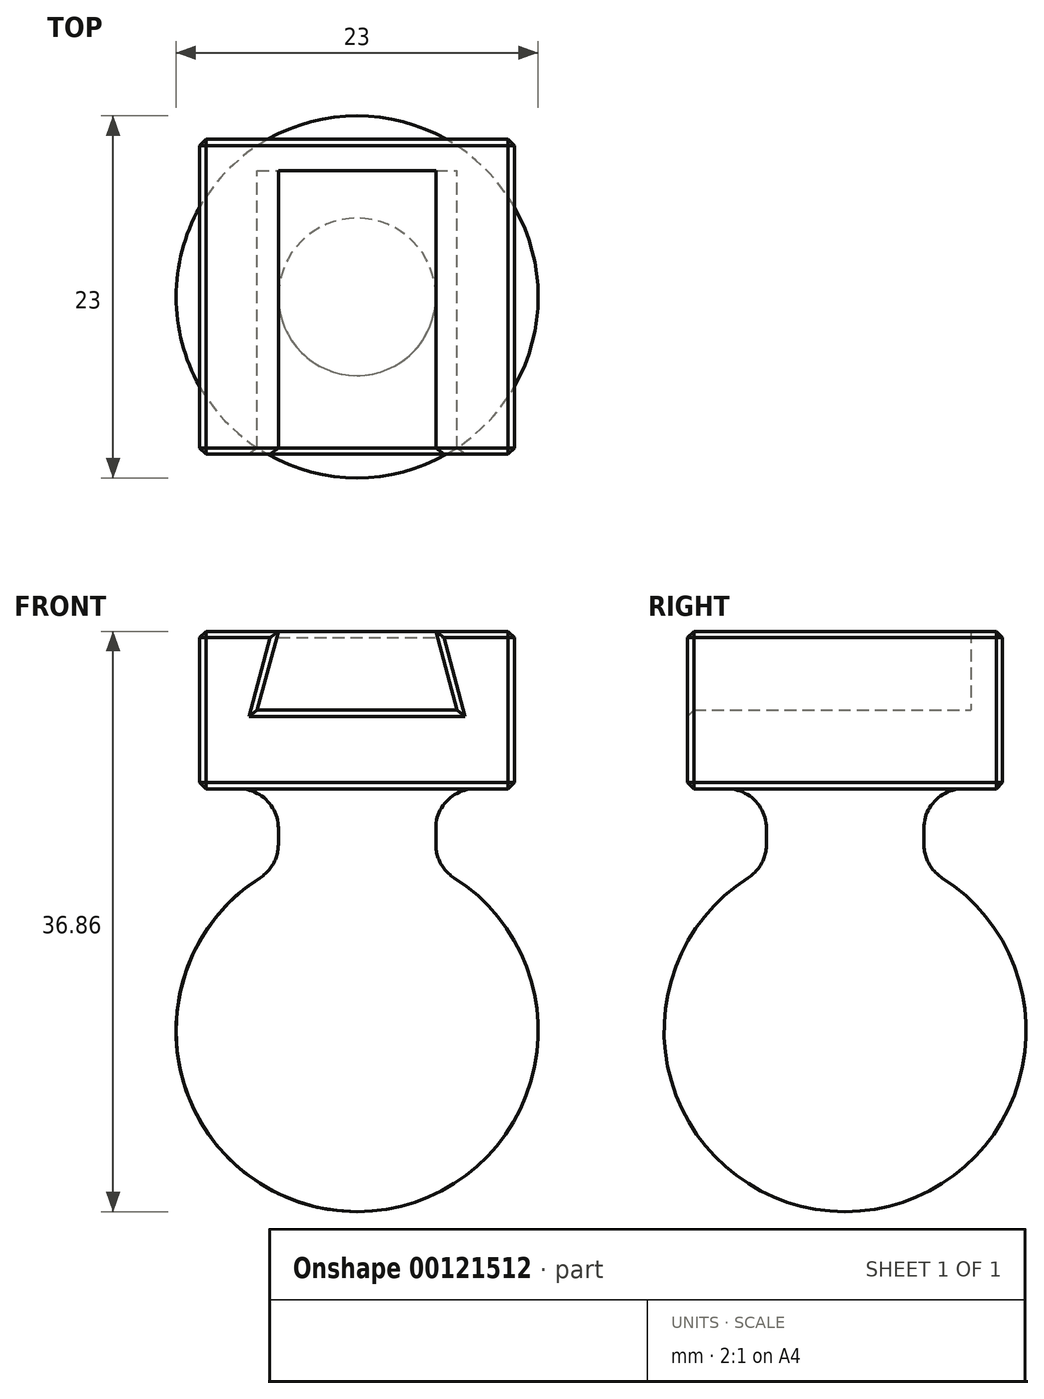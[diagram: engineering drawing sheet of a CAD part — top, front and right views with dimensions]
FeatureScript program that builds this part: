
annotation { "Feature Type Name" : "Feature", "Feature Type Description" : "" }
export const myFeature = defineFeature(function(context is Context, id is Id, definition is map)
    precondition{}
    {
        {
            assignVariable(context, id + "F0", {"name" : "PrintOffset", "anyValue" : 0.4});
        }
        {
            assignVariable(context, id + "F1", {"name" : "DovetailBackstopDepth", "anyValue" : 2});
        }
        {
            assignVariable(context, id + "F2", {"name" : "DovetailDepth", "anyValue" : 20});
        }
        {
            var Q0;
            Q0=qCreatedBy(makeId("Front.planeOp"),FACE);
            var sketch = newSketch(context, id + "F3", { "sketchPlane" : qUnion([Q0])});
            skCircle(sketch, "E0", {"center": v(0, 11.5) * mm, "radius": 11.5 * mm});
            skLineSegment(sketch, "E1", {"start": v(5, 21.86) * mm, "end": v(5, 26.86) * mm});
            skLineSegment(sketch, "E2", {"start": v(0, 26.86) * mm, "end": v(0, 62.06) * mm, "construction": true});
            skLineSegment(sketch, "E3.MirrorCS", {"start": v(-5, 21.86) * mm, "end": v(-5, 26.86) * mm});
            skLineSegment(sketch, "E4", {"start": v(-10, 26.86) * mm, "end": v(10, 26.86) * mm});
            skPoint(sketch, "E5", {"position": v(0, 26.86) * mm});
            skLineSegment(sketch, "E6", {"start": v(0, 26.86) * mm, "end": v(0, 0) * mm});
            skLineSegment(sketch, "E7", {"start": v(-6.34, 31.86) * mm, "end": v(6.34, 31.86) * mm});
            skLineSegment(sketch, "E8", {"start": v(-10, 26.86) * mm, "end": v(-10, 36.86) * mm});
            skLineSegment(sketch, "E9", {"start": v(-10, 36.86) * mm, "end": v(-5, 36.86) * mm});
            skLineSegment(sketch, "E10", {"start": v(-5, 36.86) * mm, "end": v(-6.34, 31.86) * mm});
            skLineSegment(sketch, "E11.MirrorCS", {"start": v(5, 36.86) * mm, "end": v(6.34, 31.86) * mm});
            skLineSegment(sketch, "E12.MirrorCS", {"start": v(10, 26.86) * mm, "end": v(10, 36.86) * mm});
            skLineSegment(sketch, "E13.MirrorCS", {"start": v(10, 36.86) * mm, "end": v(5, 36.86) * mm});
            skLineSegment(sketch, "E14", {"start": v(-5, 36.86) * mm, "end": v(5, 36.86) * mm});
            skSolve(sketch);
        }
        {
            var Q0;
            {var subQ2=sQuery(id+"F3.wireOp",EDGE,"E6");Q0=makeQuery(id+"F3.imprint","IMPRINT",FACE,{"disambiguationData":[TD([[makeQuery(id+"F3.imprint","IMPRINT",EDGE,{"derivedFrom":subQ2}),-1.0]])]});}
            var Q1;
            Q1=sQuery(id+"F3.wireOp",EDGE,"E6");
            revolve(context, id + "F4", {"entities" : qUnion([Q0]), "axis" : qUnion([Q1]), "revolveType" : RevolveType.FULL});
        }
        {
            var Q0;
            {var subQ0=sQuery(id+"F3.wireOp",EDGE,"E3.MirrorCS");Q0=makeQuery(id+"F3.imprint","IMPRINT",FACE,{"disambiguationData":[TD([[makeQuery(id+"F3.imprint","IMPRINT",EDGE,{"derivedFrom":subQ0}),-1.0]])]});}
            var Q1;
            Q1=sQuery(id+"F3.wireOp",EDGE,"E6");
            revolve(context, id + "F5", {"operationType" : NewBodyOperationType.ADD, "entities" : qUnion([Q0]), "axis" : qUnion([Q1]), "revolveType" : RevolveType.FULL});
        }
        {
            var Q0;
            Q0=makeQuery(id+"F3.imprint","IMPRINT",FACE,{"disambiguationData":[TD([[makeQuery(id+"F3.imprint","IMPRINT",EDGE,{"derivedFrom":sQuery(id+"F3.wireOp",EDGE,"E7")}),-1.0]])]});
            extrude(context, id + "F6", {"entities" : qUnion([Q0]), "operationType" : NewBodyOperationType.ADD, "endBound" : BoundingType.SYMMETRIC, "depth" : (getVariable(context, 'DovetailDepth')) * mm});
        }
        {
            var Q0;
            Q0=makeQuery(id+"F3.imprint","IMPRINT",FACE,{"disambiguationData":[TD([[makeQuery(id+"F3.imprint","IMPRINT",EDGE,{"derivedFrom":sQuery(id+"F3.wireOp",EDGE,"E7")}),1.0]])]});
            extrude(context, id + "F7", {"entities" : qUnion([Q0]), "operationType" : NewBodyOperationType.ADD, "oppositeDirection" : true, "depth" : (getVariable(context, 'DovetailDepth') / 2) * mm, "hasSecondDirection" : true, "secondDirectionOppositeDirection" : true, "secondDirectionDepth" : (getVariable(context, 'DovetailDepth') / 2 - getVariable(context, 'DovetailBackstopDepth')) * mm});
        }
        {
            var Q0;
            Q0=makeQuery(id+"F5.opRevolve","SWEPT_FACE",FACE,{"disambiguationData":[OSD([sQuery(id+"F3.wireOp",EDGE,"E3.MirrorCS")])]});
            fillet(context, id + "F9", {"entities" : qUnion([Q0]), "radius" : 2.5 * mm, "tangentPropagation" : true, "allowEdgeOverflow" : false});
        }
        {
            var Q0;
            Q0=makeQuery(id+"F6.opExtrude","CAP_FACE",FACE,{"disambiguationData":[OSD([sQuery(id+"F3.wireOp",EDGE,"E4"),sQuery(id+"F3.wireOp",EDGE,"E7"),sQuery(id+"F3.wireOp",EDGE,"E8"),sQuery(id+"F3.wireOp",EDGE,"E9"),sQuery(id+"F3.wireOp",EDGE,"E10"),sQuery(id+"F3.wireOp",EDGE,"E11.MirrorCS"),sQuery(id+"F3.wireOp",EDGE,"E12.MirrorCS"),sQuery(id+"F3.wireOp",EDGE,"E13.MirrorCS")])],"isStart":false});
            var Q1;
            Q1=makeQuery(id+"F6.opExtrude","SWEPT_FACE",FACE,{"disambiguationData":[OSD([sQuery(id+"F3.wireOp",EDGE,"E12.MirrorCS")])]});
            var Q2;
            Q2=makeQuery(id+"F6.opExtrude","SWEPT_FACE",FACE,{"disambiguationData":[OSD([sQuery(id+"F3.wireOp",EDGE,"E4")])]});
            var Q3;
            Q3=makeQuery(id+"F6.opExtrude","SWEPT_FACE",FACE,{"disambiguationData":[OSD([sQuery(id+"F3.wireOp",EDGE,"E8")])]});
            var Q4;
            {var subQ0=sQuery(id+"F3.wireOp",EDGE,"E11.MirrorCS");var subQ1=sQuery(id+"F3.wireOp",EDGE,"E10");var subQ2=sQuery(id+"F3.wireOp",EDGE,"E7");Q4=makeQuery(id+"F7.boolean.opBoolean","MERGE",FACE,{"derivedFrom":[makeQuery(id+"F6.opExtrude","CAP_FACE",FACE,{"disambiguationData":[OSD([sQuery(id+"F3.wireOp",EDGE,"E4"),subQ2,sQuery(id+"F3.wireOp",EDGE,"E8"),sQuery(id+"F3.wireOp",EDGE,"E9"),subQ1,subQ0,sQuery(id+"F3.wireOp",EDGE,"E12.MirrorCS"),sQuery(id+"F3.wireOp",EDGE,"E13.MirrorCS")])],"isStart":true}),makeQuery(id+"F7.opExtrude","CAP_FACE",FACE,{"disambiguationData":[OSD([subQ2,subQ1,subQ0,sQuery(id+"F3.wireOp",EDGE,"E14")])],"isStart":false})]});}
            chamfer(context, id + "F8", {"entities" : qUnion([Q0, Q1, Q2, Q3, Q4]), "width" : (getVariable(context, 'PrintOffset')) * mm, "tangentPropagation" : true});
        }
    });
